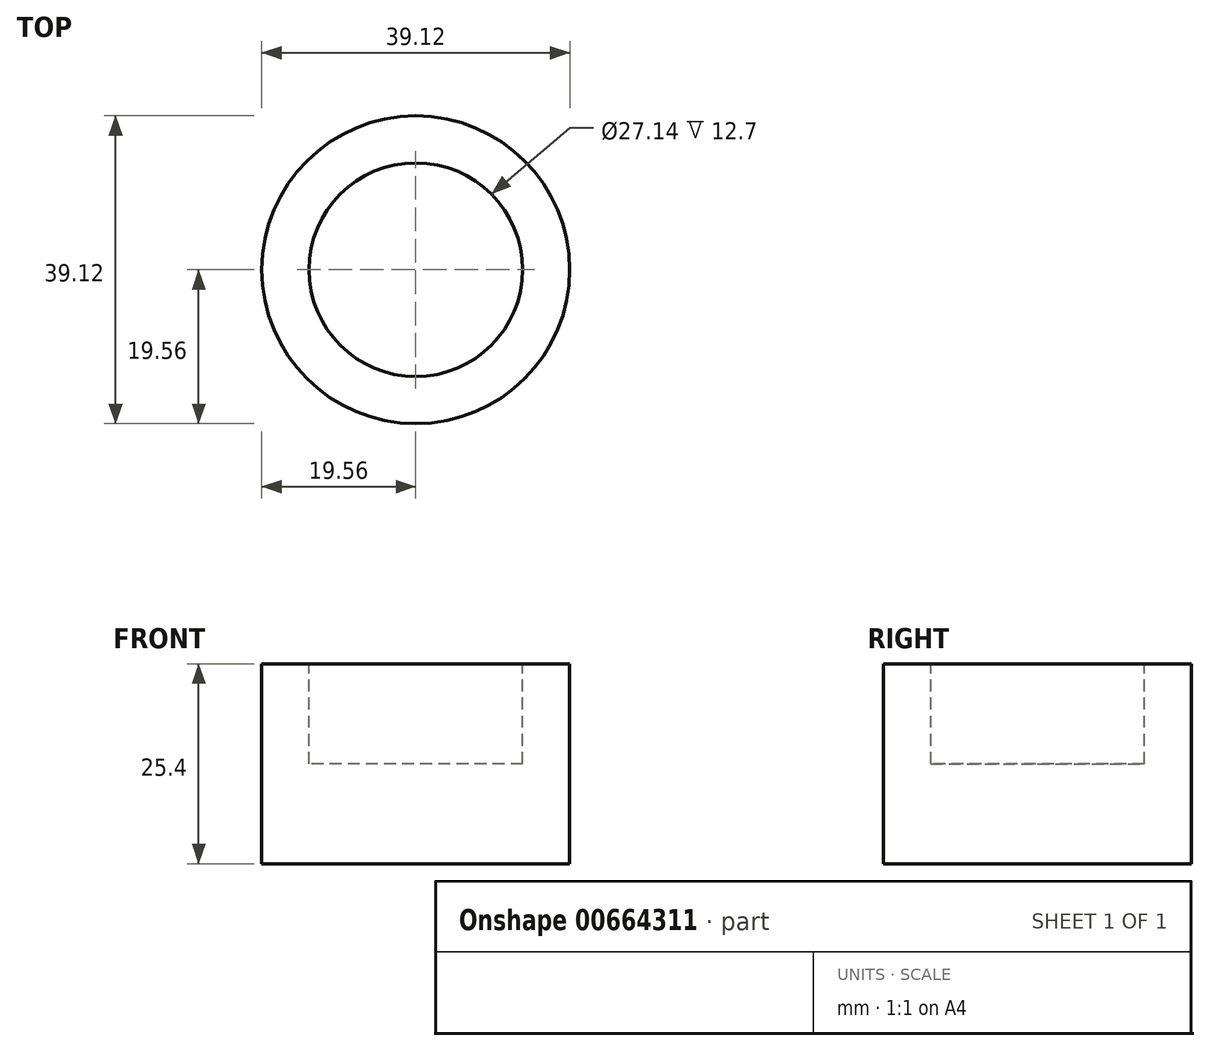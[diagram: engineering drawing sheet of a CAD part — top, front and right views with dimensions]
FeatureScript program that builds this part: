
annotation { "Feature Type Name" : "Feature", "Feature Type Description" : "" }
export const myFeature = defineFeature(function(context is Context, id is Id, definition is map)
    precondition{}
    {
        {
            var Q0;
            Q0=qCreatedBy(makeId("Top.planeOp"),FACE);
            var sketch = newSketch(context, id + "F0", { "sketchPlane" : qUnion([Q0])});
            skCircle(sketch, "E0", {"center": v(0, 0) * mm, "radius": 19.56 * mm});
            skSolve(sketch);
        }
        {
            var Q0;
            Q0=makeQuery(id+"F0.imprint","IMPRINT",FACE,{"disambiguationData":[TD([[makeQuery(id+"F0.imprint","IMPRINT",EDGE,{"derivedFrom":sQuery(id+"F0.wireOp",EDGE,"E0")}),1.0]])]});
            extrude(context, id + "F1", {"entities" : qUnion([Q0]), "depth" : 25.4 * mm, "offsetDistance" : 25.4 * mm});
        }
        {
            var Q0;
            Q0=qCreatedBy(makeId("Front.planeOp"),FACE);
            var sketch = newSketch(context, id + "F2", { "sketchPlane" : qUnion([Q0])});
            skLineSegment(sketch, "E1", {"start": v(0, 0) * mm, "end": v(0, -77.43) * mm});
            skSolve(sketch);
        }
        {
            var Q0;
            Q0=qCreatedBy(makeId("Front.planeOp"),FACE);
            var sketch = newSketch(context, id + "F3", { "sketchPlane" : qUnion([Q0])});
            skLineSegment(sketch, "E2", {"start": v(0, -77.19) * mm, "end": v(-19.05, 0) * mm});
            skSolve(sketch);
        }
        {
            var Q0;
            Q0=sQuery(id+"F3.wireOp",EDGE,"E2");
            var Q1;
            Q1=sQuery(id+"F2.wireOp",EDGE,"E1");
            revolve(context, id + "F4", {"bodyType" : ToolBodyType.SURFACE, "surfaceEntities" : qUnion([Q0]), "axis" : qUnion([Q1]), "revolveType" : RevolveType.FULL});
        }
        {
            var Q0;
            Q0=makeQuery(id+"F1.opExtrude","CAP_FACE",FACE,{"disambiguationData":[OSD([sQuery(id+"F0.wireOp",EDGE,"E0")])],"isStart":false});
            var sketch = newSketch(context, id + "F5", { "sketchPlane" : qUnion([Q0])});
            skCircle(sketch, "E3", {"center": v(0, 0) * mm, "radius": 13.57 * mm});
            skSolve(sketch);
        }
        {
            var Q0;
            Q0=makeQuery(id+"F5.imprint","IMPRINT",FACE,{"disambiguationData":[TD([[makeQuery(id+"F5.imprint","IMPRINT",EDGE,{"derivedFrom":sQuery(id+"F5.wireOp",EDGE,"E3")}),1.0]])]});
            extrude(context, id + "F6", {"entities" : qUnion([Q0]), "operationType" : NewBodyOperationType.REMOVE, "oppositeDirection" : true, "depth" : 12.7 * mm, "offsetDistance" : 25.4 * mm});
        }
    });
